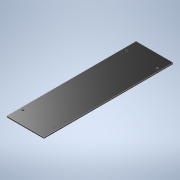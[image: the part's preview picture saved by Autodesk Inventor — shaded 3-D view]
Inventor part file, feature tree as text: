
AUTODESK INVENTOR PART (.ipt)
format: ipt  version: 2022 (Build 260153000, 153)  size: 112,640 bytes
history: native  units: mm
features: sketch x2, other x1, extrude x1, hole x1
ambient origin geometry x8: Origin, YZ Plane, XZ Plane, XY Plane, X Axis, Y Axis, Z Axis, Center Point
bodies: Body1 (feature_tree)
feature tree (5):
  other  "ソリッド1"
  extrude  "押し出し1"  Depth=200.0mm
  hole  "穴1"  [1 undecoded]
  sketch  "スケッチ1"
  sketch  "スケッチ3"
note: 1 required parameter value undecoded (feature->parameter linkage not recoverable at this tier; creation-order binding heuristic only, values carry confidence <= 0.55)
